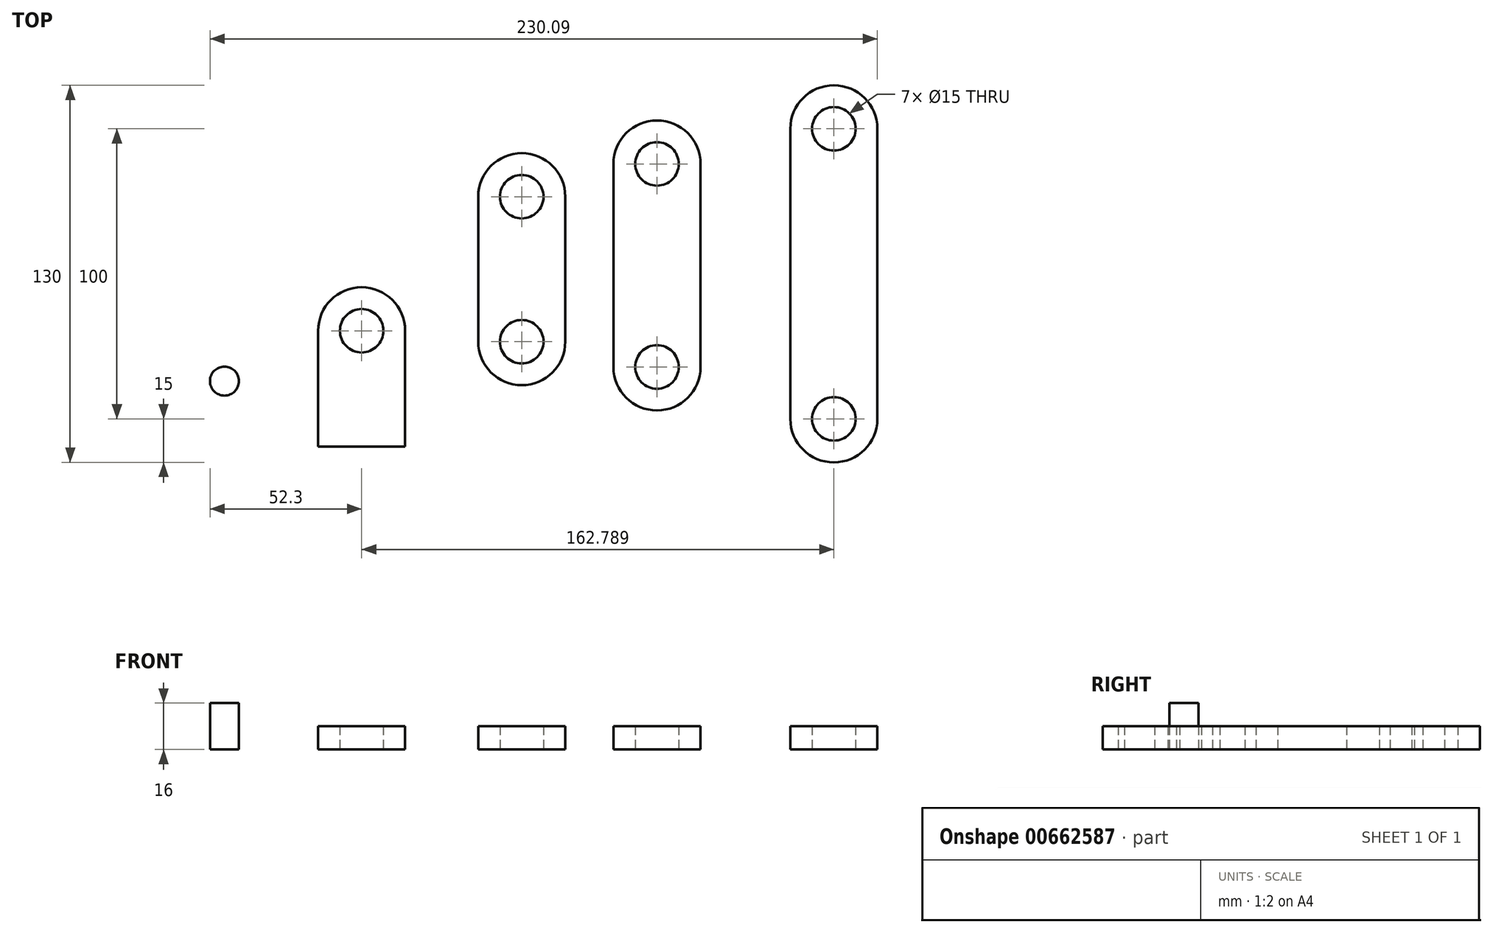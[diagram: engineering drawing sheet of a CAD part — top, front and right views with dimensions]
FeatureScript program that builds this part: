
annotation { "Feature Type Name" : "Feature", "Feature Type Description" : "" }
export const myFeature = defineFeature(function(context is Context, id is Id, definition is map)
    precondition{}
    {
        {
            var Q0;
            Q0=qCreatedBy(makeId("Top.planeOp"),FACE);
            var sketch = newSketch(context, id + "F0", { "sketchPlane" : qUnion([Q0])});
            skArc(sketch, "E0", {"start": v(15, 40) * mm, "mid": v(0, 55) * mm, "end": v(-15, 40) * mm});
            skLineSegment(sketch, "E1", {"start": v(-15, 40) * mm, "end": v(-15, 0) * mm});
            skLineSegment(sketch, "E2", {"start": v(-15, 0) * mm, "end": v(15, 0) * mm});
            skLineSegment(sketch, "E3", {"start": v(15, 0) * mm, "end": v(15, 40) * mm});
            skCircle(sketch, "E4", {"center": v(0, 40) * mm, "radius": 7.5 * mm});
            skSolve(sketch);
        }
        {
            var Q0;
            Q0=makeQuery(id+"F0.imprint","IMPRINT",FACE,{"disambiguationData":[TD([[makeQuery(id+"F0.imprint","IMPRINT",EDGE,{"derivedFrom":sQuery(id+"F0.wireOp",EDGE,"E0")}),1.0]])]});
            extrude(context, id + "F1", {"entities" : qUnion([Q0]), "depth" : 8 * mm, "offsetDistance" : 25 * mm});
        }
        {
            var Q0;
            Q0=qCreatedBy(makeId("Top.planeOp"),FACE);
            var sketch = newSketch(context, id + "F2", { "sketchPlane" : qUnion([Q0])});
            skArc(sketch, "E5", {"start": v(70.18, 86.22) * mm, "mid": v(55.18, 101.22) * mm, "end": v(40.18, 86.22) * mm});
            skArc(sketch, "E6", {"start": v(40.18, 36.22) * mm, "mid": v(55.18, 21.22) * mm, "end": v(70.18, 36.22) * mm});
            skLineSegment(sketch, "E7", {"start": v(40.18, 86.22) * mm, "end": v(40.18, 36.22) * mm});
            skLineSegment(sketch, "E8", {"start": v(70.18, 86.22) * mm, "end": v(70.18, 36.22) * mm});
            skCircle(sketch, "E9", {"center": v(55.18, 86.22) * mm, "radius": 7.5 * mm});
            skCircle(sketch, "E10", {"center": v(55.18, 36.22) * mm, "radius": 7.5 * mm});
            skSolve(sketch);
        }
        {
            var Q0;
            Q0=makeQuery(id+"F2.imprint","IMPRINT",FACE,{"disambiguationData":[TD([[makeQuery(id+"F2.imprint","IMPRINT",EDGE,{"derivedFrom":sQuery(id+"F2.wireOp",EDGE,"E5")}),1.0]])]});
            extrude(context, id + "F3", {"entities" : qUnion([Q0]), "depth" : 8 * mm, "offsetDistance" : 25 * mm});
        }
        {
            var Q0;
            Q0=qCreatedBy(makeId("Top.planeOp"),FACE);
            var sketch = newSketch(context, id + "F4", { "sketchPlane" : qUnion([Q0])});
            skArc(sketch, "E11", {"start": v(86.81, 27.52) * mm, "mid": v(101.81, 12.52) * mm, "end": v(116.81, 27.52) * mm});
            skArc(sketch, "E12", {"start": v(116.81, 97.52) * mm, "mid": v(101.81, 112.52) * mm, "end": v(86.81, 97.52) * mm});
            skLineSegment(sketch, "E13", {"start": v(86.81, 97.52) * mm, "end": v(86.81, 27.52) * mm});
            skLineSegment(sketch, "E14", {"start": v(116.81, 97.52) * mm, "end": v(116.81, 27.52) * mm});
            skCircle(sketch, "E15", {"center": v(101.81, 97.52) * mm, "radius": 7.5 * mm});
            skCircle(sketch, "E16", {"center": v(101.81, 27.52) * mm, "radius": 7.5 * mm});
            skSolve(sketch);
        }
        {
            var Q0;
            Q0 = qSketchRegion(id + "F4", true);
            extrude(context, id + "F5", {"entities" : qUnion([Q0]), "depth" : 8 * mm, "offsetDistance" : 25 * mm});
        }
        {
            var Q0;
            Q0=qCreatedBy(makeId("Top.planeOp"),FACE);
            var sketch = newSketch(context, id + "F6", { "sketchPlane" : qUnion([Q0])});
            skArc(sketch, "E17", {"start": v(177.79, 109.62) * mm, "mid": v(162.79, 124.62) * mm, "end": v(147.79, 109.62) * mm});
            skArc(sketch, "E18", {"start": v(147.79, 9.62) * mm, "mid": v(162.79, -5.38) * mm, "end": v(177.79, 9.62) * mm});
            skLineSegment(sketch, "E19", {"start": v(147.79, 109.62) * mm, "end": v(147.79, 9.62) * mm});
            skLineSegment(sketch, "E20", {"start": v(177.79, 109.62) * mm, "end": v(177.79, 9.62) * mm});
            skCircle(sketch, "E21", {"center": v(162.79, 109.62) * mm, "radius": 7.5 * mm});
            skCircle(sketch, "E22", {"center": v(162.79, 9.62) * mm, "radius": 7.5 * mm});
            skSolve(sketch);
        }
        {
            var Q0;
            Q0=makeQuery(id+"F6.imprint","IMPRINT",FACE,{"disambiguationData":[TD([[makeQuery(id+"F6.imprint","IMPRINT",EDGE,{"derivedFrom":sQuery(id+"F6.wireOp",EDGE,"E17")}),1.0]])]});
            extrude(context, id + "F7", {"entities" : qUnion([Q0]), "depth" : 8 * mm, "offsetDistance" : 25 * mm});
        }
        {
            var Q0;
            Q0=qCreatedBy(makeId("Top.planeOp"),FACE);
            var sketch = newSketch(context, id + "F8", { "sketchPlane" : qUnion([Q0])});
            skCircle(sketch, "E23", {"center": v(-47.3, 22.64) * mm, "radius": 5 * mm});
            skSolve(sketch);
        }
        {
            var Q0;
            Q0=makeQuery(id+"F8.imprint","IMPRINT",FACE,{"disambiguationData":[TD([[makeQuery(id+"F8.imprint","IMPRINT",EDGE,{"derivedFrom":sQuery(id+"F8.wireOp",EDGE,"E23")}),1.0]])]});
            extrude(context, id + "F9", {"entities" : qUnion([Q0]), "depth" : 16 * mm, "offsetDistance" : 25 * mm});
        }
    });
